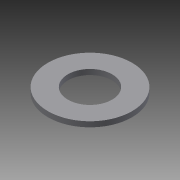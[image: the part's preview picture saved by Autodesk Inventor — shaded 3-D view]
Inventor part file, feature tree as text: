
AUTODESK INVENTOR PART (.ipt)
format: ipt  version: 2013 (Build 170138000, 138)  size: 72,704 bytes
history: native  units: mm
features: extrude x1, sketch x1
ambient origin geometry x8: Origin, YZ Plane, XZ Plane, XY Plane, X Axis, Y Axis, Z Axis, Center Point
bodies: Solid1 (feature_tree)
feature tree (2):
  extrude  "Extrusion1"  Depth=16.0mm
  sketch  "Sketch1"  dims[d0=8.4mm d2=16.0mm d3=1.0mm d4=0.0mm]
